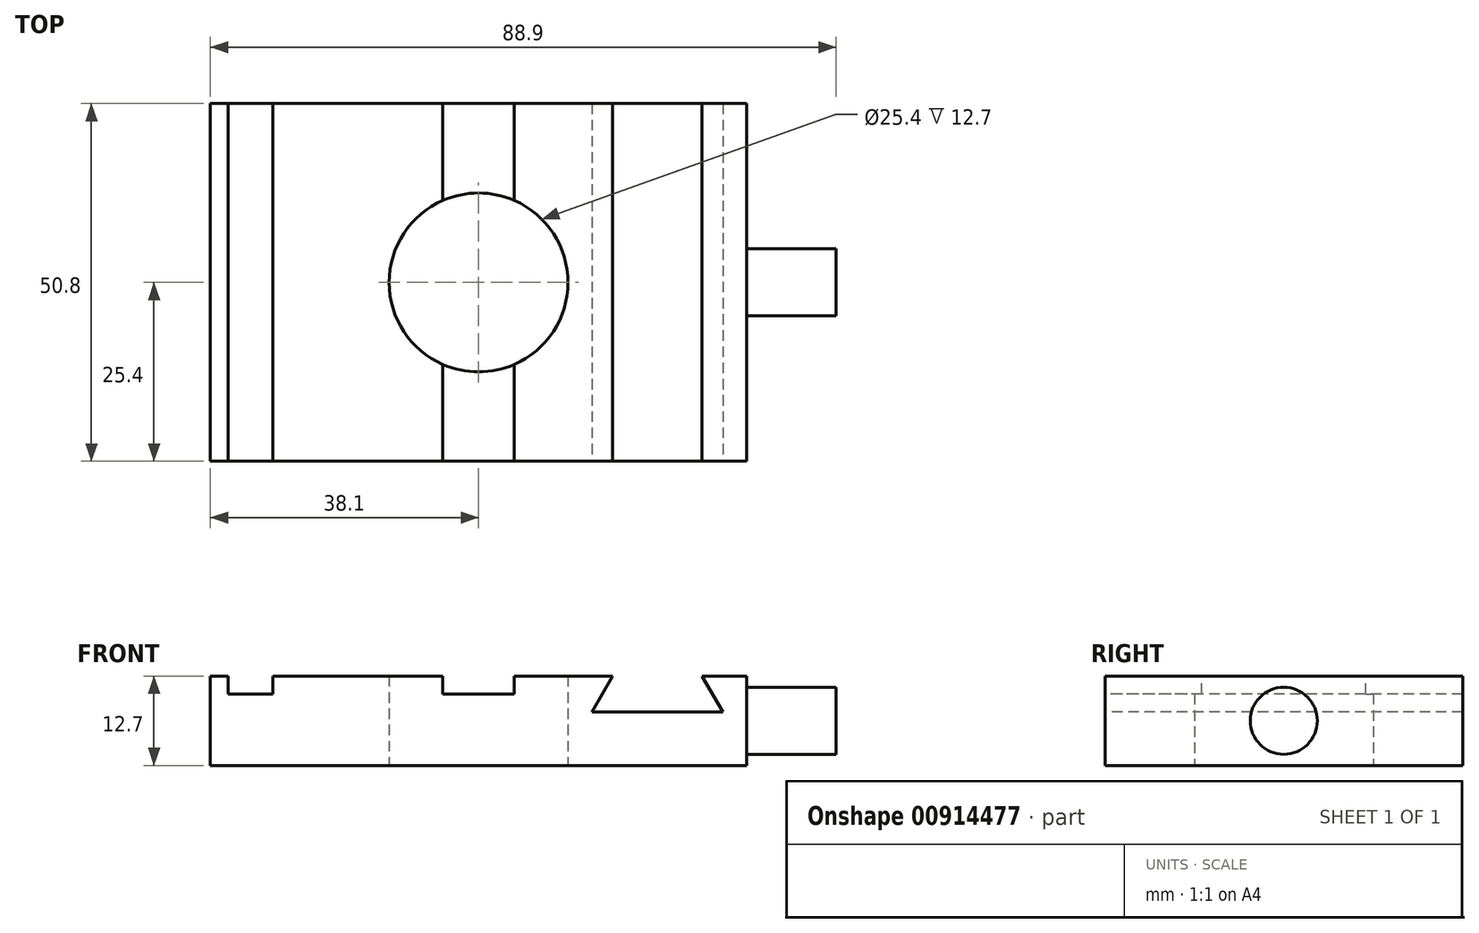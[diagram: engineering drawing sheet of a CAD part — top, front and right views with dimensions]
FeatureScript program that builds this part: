
annotation { "Feature Type Name" : "Feature", "Feature Type Description" : "" }
export const myFeature = defineFeature(function(context is Context, id is Id, definition is map)
    precondition{}
    {
        {
            var Q0;
            Q0=qCreatedBy(makeId("Top.planeOp"),FACE);
            var sketch = newSketch(context, id + "F0", { "sketchPlane" : qUnion([Q0])});
            skLineSegment(sketch, "E0.bottom", {"start": v(38.1, -25.4) * mm, "end": v(-38.1, -25.4) * mm});
            skLineSegment(sketch, "E0.top", {"start": v(38.1, 25.4) * mm, "end": v(-38.1, 25.4) * mm});
            skLineSegment(sketch, "E0.left", {"start": v(38.1, -25.4) * mm, "end": v(38.1, 25.4) * mm});
            skLineSegment(sketch, "E0.right", {"start": v(-38.1, -25.4) * mm, "end": v(-38.1, 25.4) * mm});
            skPoint(sketch, "E0.middle", {"position": v(0, 0) * mm});
            skCircle(sketch, "E1", {"center": v(0, 0) * mm, "radius": 12.7 * mm});
            skSolve(sketch);
        }
        {
            var Q0;
            Q0=makeQuery(id+"F0.imprint","IMPRINT",FACE,{"disambiguationData":[TD([[makeQuery(id+"F0.imprint","IMPRINT",EDGE,{"derivedFrom":sQuery(id+"F0.wireOp",EDGE,"E0.bottom")}),-1.0]])]});
            extrude(context, id + "F1", {"entities" : qUnion([Q0]), "depth" : 12.7 * mm, "offsetDistance" : 25.4 * mm});
        }
        {
            var Q0;
            Q0=makeQuery(id+"F1.opExtrude","CAP_FACE",FACE,{"disambiguationData":[OSD([sQuery(id+"F0.wireOp",EDGE,"E0.bottom"),sQuery(id+"F0.wireOp",EDGE,"E0.top"),sQuery(id+"F0.wireOp",EDGE,"E0.left"),sQuery(id+"F0.wireOp",EDGE,"E0.right"),sQuery(id+"F0.wireOp",EDGE,"E1")])],"isStart":false});
            var sketch = newSketch(context, id + "F2", { "sketchPlane" : qUnion([Q0])});
            skLineSegment(sketch, "E2.bottom", {"start": v(-35.56, 25.4) * mm, "end": v(-29.21, 25.4) * mm});
            skLineSegment(sketch, "E2.top", {"start": v(-35.56, -25.4) * mm, "end": v(-29.21, -25.4) * mm});
            skLineSegment(sketch, "E2.left", {"start": v(-35.56, 25.4) * mm, "end": v(-35.56, -25.4) * mm});
            skLineSegment(sketch, "E2.right", {"start": v(-29.21, 25.4) * mm, "end": v(-29.21, -25.4) * mm});
            skLineSegment(sketch, "E3", {"start": v(-5.08, 25.4) * mm, "end": v(-5.08, -25.4) * mm});
            skLineSegment(sketch, "E4", {"start": v(-5.08, -25.4) * mm, "end": v(5.08, -25.4) * mm});
            skLineSegment(sketch, "E5", {"start": v(5.08, -25.4) * mm, "end": v(5.08, 25.4) * mm});
            skLineSegment(sketch, "E6", {"start": v(5.08, 25.4) * mm, "end": v(-5.08, 25.4) * mm});
            skPoint(sketch, "E7", {"position": v(0, 0) * mm});
            skPoint(sketch, "E8", {"position": v(-11.2, 6) * mm});
            skPoint(sketch, "E9", {"position": v(-10.86, 6.59) * mm});
            skLineSegment(sketch, "E10", {"start": v(0, 25.4) * mm, "end": v(0, -25.4) * mm, "construction": true});
            skSolve(sketch);
        }
        {
            var Q0;
            Q0=makeQuery(id+"F2.imprint","IMPRINT",FACE,{"disambiguationData":[TD([[makeQuery(id+"F2.imprint","IMPRINT",EDGE,{"derivedFrom":sQuery(id+"F2.wireOp",EDGE,"E2.bottom")}),1.0]])]});
            var Q1;
            {var subQ0=sQuery(id+"F2.wireOp",EDGE,"E4");Q1=makeQuery(id+"F2.imprint","IMPRINT",FACE,{"disambiguationData":[TD([[makeQuery(id+"F2.imprint","IMPRINT",EDGE,{"derivedFrom":subQ0}),-1.0]])]});}
            var Q2;
            {var subQ0=sQuery(id+"F2.wireOp",EDGE,"E6");Q2=makeQuery(id+"F2.imprint","IMPRINT",FACE,{"disambiguationData":[TD([[makeQuery(id+"F2.imprint","IMPRINT",EDGE,{"derivedFrom":subQ0}),1.0]])]});}
            extrude(context, id + "F3", {"entities" : qUnion([Q0, Q1, Q2]), "operationType" : NewBodyOperationType.REMOVE, "oppositeDirection" : true, "depth" : 2.54 * mm, "offsetDistance" : 25.4 * mm});
        }
        {
            var Q0;
            Q0=makeQuery(id+"F1.opExtrude","SWEPT_FACE",FACE,{"disambiguationData":[OSD([sQuery(id+"F0.wireOp",EDGE,"E0.bottom")])]});
            var sketch = newSketch(context, id + "F4", { "sketchPlane" : qUnion([Q0])});
            skLineSegment(sketch, "E11", {"start": v(19.05, 12.7) * mm, "end": v(16.12, 7.62) * mm});
            skLineSegment(sketch, "E12", {"start": v(16.12, 7.62) * mm, "end": v(34.68, 7.62) * mm});
            skLineSegment(sketch, "E13", {"start": v(34.68, 7.62) * mm, "end": v(31.75, 12.7) * mm});
            skLineSegment(sketch, "E14", {"start": v(31.75, 12.7) * mm, "end": v(19.05, 12.7) * mm});
            skLineSegment(sketch, "E15", {"start": v(25.4, 7.62) * mm, "end": v(25.4, 12.7) * mm, "construction": true});
            skSolve(sketch);
        }
        {
            var Q0;
            Q0=makeQuery(id+"F4.imprint","IMPRINT",FACE,{"disambiguationData":[TD([[makeQuery(id+"F4.imprint","IMPRINT",EDGE,{"derivedFrom":sQuery(id+"F4.wireOp",EDGE,"E11")}),1.0]])]});
            extrude(context, id + "F5", {"entities" : qUnion([Q0]), "operationType" : NewBodyOperationType.REMOVE, "endBound" : BoundingType.THROUGH_ALL, "oppositeDirection" : true, "depth" : 25.4 * mm, "offsetDistance" : 25.4 * mm});
        }
        {
            var Q0;
            Q0=makeQuery(id+"F1.opExtrude","SWEPT_FACE",FACE,{"disambiguationData":[OSD([sQuery(id+"F0.wireOp",EDGE,"E0.left")])]});
            var sketch = newSketch(context, id + "F6", { "sketchPlane" : qUnion([Q0])});
            skCircle(sketch, "E16", {"center": v(0, 6.35) * mm, "radius": 4.76 * mm});
            skPoint(sketch, "E16.centerSnap0", {"position": v(-25.4, 6.35) * mm});
            skPoint(sketch, "E16.centerSnap1", {"position": v(0, 12.7) * mm});
            skSolve(sketch);
        }
        {
            var Q0;
            Q0=makeQuery(id+"F6.imprint","IMPRINT",FACE,{"disambiguationData":[TD([[makeQuery(id+"F6.imprint","IMPRINT",EDGE,{"derivedFrom":sQuery(id+"F6.wireOp",EDGE,"E16")}),1.0]])]});
            extrude(context, id + "F7", {"entities" : qUnion([Q0]), "operationType" : NewBodyOperationType.ADD, "depth" : 12.7 * mm, "offsetDistance" : 25.4 * mm});
        }
    });
